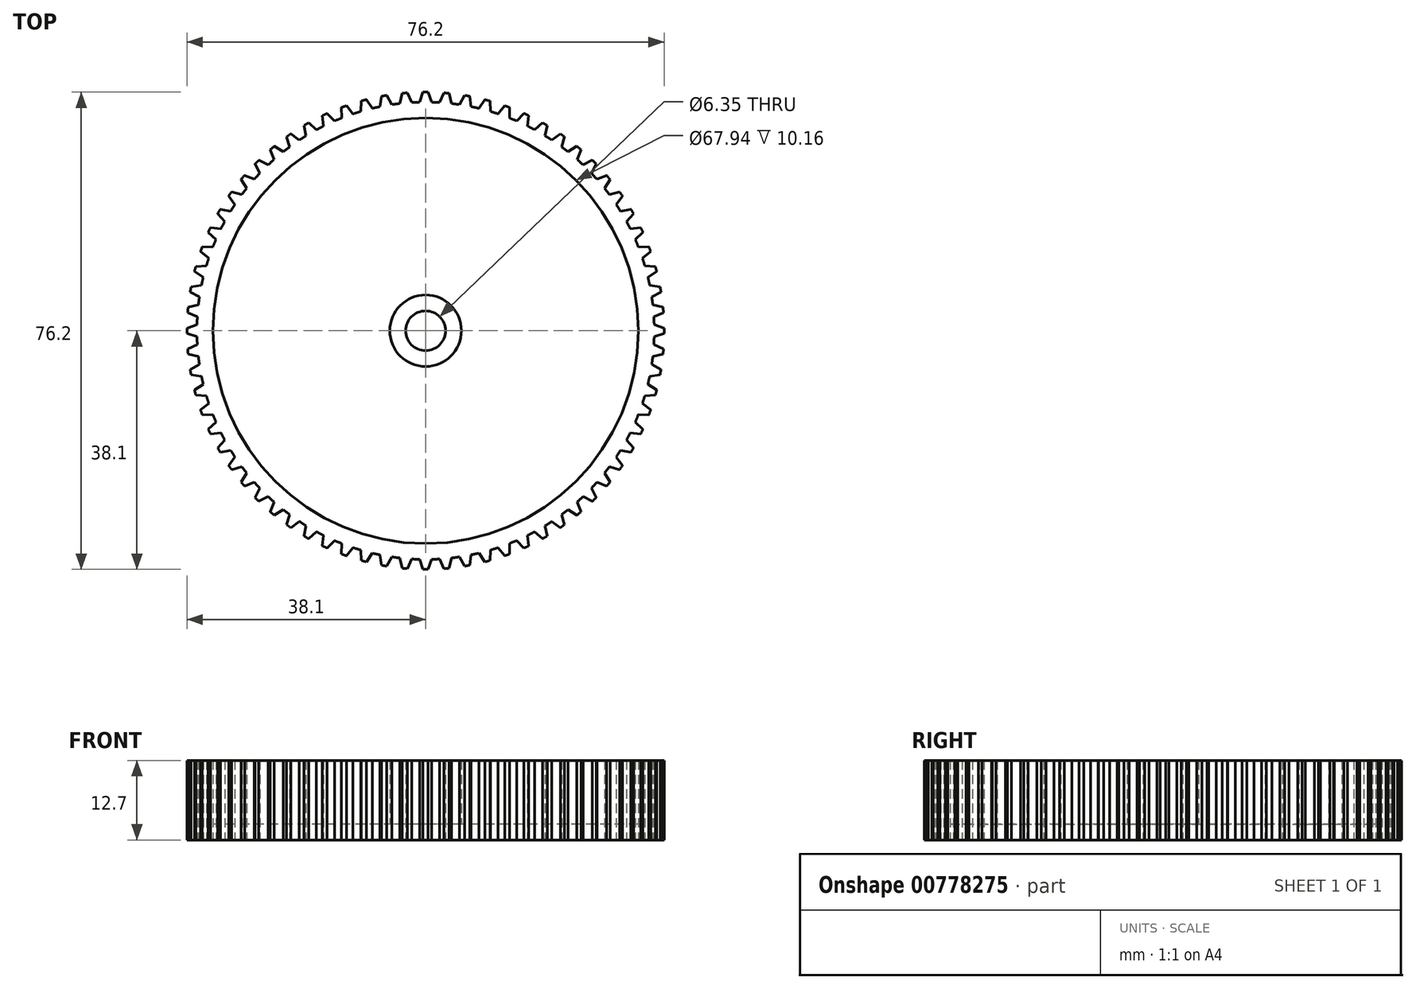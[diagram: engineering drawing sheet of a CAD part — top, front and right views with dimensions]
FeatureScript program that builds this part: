
annotation { "Feature Type Name" : "Feature", "Feature Type Description" : "" }
export const myFeature = defineFeature(function(context is Context, id is Id, definition is map)
    precondition{}
    {
        {
            var Q0;
            Q0=qCreatedBy(makeId("Top.planeOp"),FACE);
            var sketch = newSketch(context, id + "F0", { "sketchPlane" : qUnion([Q0])});
            skCircle(sketch, "E0", {"center": v(0, 0) * mm, "radius": 38.1 * mm, "construction": true});
            skCircle(sketch, "E1", {"center": v(0, 0) * mm, "radius": 3.18 * mm});
            skLineSegment(sketch, "E2", {"start": v(0, 0) * mm, "end": v(0, 49.35) * mm, "construction": true});
            skLineSegment(sketch, "E3", {"start": v(0, 0) * mm, "end": v(-2.1, 47.97) * mm, "construction": true});
            skLineSegment(sketch, "E4", {"start": v(0, 0) * mm, "end": v(2.15, 49.24) * mm, "construction": true});
            skArc(sketch, "E5", {"start": v(-1.6, 36.48) * mm, "mid": v(-1.27, 36.5) * mm, "end": v(-0.96, 36.5) * mm});
            skArc(sketch, "E6", {"start": v(1.6, 36.48) * mm, "mid": v(1.27, 36.5) * mm, "end": v(0.96, 36.5) * mm});
            skLineSegment(sketch, "E7", {"start": v(-0.96, 36.5) * mm, "end": v(-0.42, 38.1) * mm});
            skLineSegment(sketch, "E8", {"start": v(0.96, 36.5) * mm, "end": v(0.42, 38.1) * mm});
            skArc(sketch, "E9", {"start": v(0.42, 38.1) * mm, "mid": v(0, 38.1) * mm, "end": v(-0.42, 38.1) * mm});
            skLineSegment(sketch, "E10", {"start": v(0, 0) * mm, "end": v(-0.96, 36.5) * mm, "construction": true});
            skLineSegment(sketch, "E11", {"start": v(0.96, 36.5) * mm, "end": v(0, 0) * mm, "construction": true});
            skArc(sketch, "E12.1.0", {"start": v(-4.77, 36.2) * mm, "mid": v(-4.45, 36.24) * mm, "end": v(-4.13, 36.28) * mm});
            skArc(sketch, "E12.1.1", {"start": v(-2.9, 37.99) * mm, "mid": v(-3.32, 37.95) * mm, "end": v(-3.74, 37.92) * mm});
            skLineSegment(sketch, "E12.1.2", {"start": v(-4.13, 36.28) * mm, "end": v(-3.74, 37.92) * mm});
            skLineSegment(sketch, "E12.1.3", {"start": v(-2.23, 36.44) * mm, "end": v(-2.9, 37.99) * mm});
            skArc(sketch, "E12.1.4", {"start": v(-1.6, 36.48) * mm, "mid": v(-1.91, 36.46) * mm, "end": v(-2.23, 36.44) * mm});
            skArc(sketch, "E12.2.0", {"start": v(-7.9, 35.65) * mm, "mid": v(-7.6, 35.71) * mm, "end": v(-7.28, 35.78) * mm});
            skArc(sketch, "E12.2.1", {"start": v(-6.2, 37.6) * mm, "mid": v(-6.62, 37.52) * mm, "end": v(-7.03, 37.45) * mm});
            skLineSegment(sketch, "E12.2.2", {"start": v(-7.28, 35.78) * mm, "end": v(-7.03, 37.45) * mm});
            skLineSegment(sketch, "E12.2.3", {"start": v(-5.4, 36.11) * mm, "end": v(-6.2, 37.6) * mm});
            skArc(sketch, "E12.2.4", {"start": v(-4.77, 36.2) * mm, "mid": v(-5.08, 36.16) * mm, "end": v(-5.4, 36.11) * mm});
            skArc(sketch, "E12.3.0", {"start": v(-10.98, 34.82) * mm, "mid": v(-10.68, 34.92) * mm, "end": v(-10.37, 35) * mm});
            skArc(sketch, "E12.3.1", {"start": v(-9.45, 36.9) * mm, "mid": v(-9.86, 36.8) * mm, "end": v(-10.27, 36.7) * mm});
            skLineSegment(sketch, "E12.3.2", {"start": v(-10.37, 35) * mm, "end": v(-10.27, 36.7) * mm});
            skLineSegment(sketch, "E12.3.3", {"start": v(-8.52, 35.5) * mm, "end": v(-9.45, 36.9) * mm});
            skArc(sketch, "E12.3.4", {"start": v(-7.9, 35.65) * mm, "mid": v(-8.21, 35.58) * mm, "end": v(-8.52, 35.5) * mm});
            skArc(sketch, "E12.4.0", {"start": v(-13.97, 33.73) * mm, "mid": v(-13.68, 33.85) * mm, "end": v(-13.38, 33.97) * mm});
            skArc(sketch, "E12.4.1", {"start": v(-12.63, 35.94) * mm, "mid": v(-13.03, 35.8) * mm, "end": v(-13.43, 35.66) * mm});
            skLineSegment(sketch, "E12.4.2", {"start": v(-13.38, 33.97) * mm, "end": v(-13.43, 35.66) * mm});
            skLineSegment(sketch, "E12.4.3", {"start": v(-11.59, 34.63) * mm, "end": v(-12.63, 35.94) * mm});
            skArc(sketch, "E12.4.4", {"start": v(-10.98, 34.82) * mm, "mid": v(-11.28, 34.73) * mm, "end": v(-11.59, 34.63) * mm});
            skArc(sketch, "E12.5.0", {"start": v(-16.86, 32.39) * mm, "mid": v(-16.58, 32.53) * mm, "end": v(-16.3, 32.68) * mm});
            skArc(sketch, "E12.5.1", {"start": v(-15.72, 34.7) * mm, "mid": v(-16.1, 34.53) * mm, "end": v(-16.48, 34.35) * mm});
            skLineSegment(sketch, "E12.5.2", {"start": v(-16.3, 32.68) * mm, "end": v(-16.48, 34.35) * mm});
            skLineSegment(sketch, "E12.5.3", {"start": v(-14.56, 33.48) * mm, "end": v(-15.72, 34.7) * mm});
            skArc(sketch, "E12.5.4", {"start": v(-13.97, 33.73) * mm, "mid": v(-14.27, 33.6) * mm, "end": v(-14.56, 33.48) * mm});
            skArc(sketch, "E12.6.0", {"start": v(-19.62, 30.8) * mm, "mid": v(-19.35, 30.96) * mm, "end": v(-19.08, 31.13) * mm});
            skArc(sketch, "E12.6.1", {"start": v(-18.68, 33.2) * mm, "mid": v(-19.05, 33) * mm, "end": v(-19.41, 32.78) * mm});
            skLineSegment(sketch, "E12.6.2", {"start": v(-19.08, 31.13) * mm, "end": v(-19.41, 32.78) * mm});
            skLineSegment(sketch, "E12.6.3", {"start": v(-17.42, 32.09) * mm, "end": v(-18.68, 33.2) * mm});
            skArc(sketch, "E12.6.4", {"start": v(-16.86, 32.39) * mm, "mid": v(-17.14, 32.24) * mm, "end": v(-17.42, 32.09) * mm});
            skArc(sketch, "E12.7.0", {"start": v(-22.23, 28.97) * mm, "mid": v(-21.97, 29.16) * mm, "end": v(-21.72, 29.35) * mm});
            skArc(sketch, "E12.7.1", {"start": v(-21.5, 31.45) * mm, "mid": v(-21.85, 31.2) * mm, "end": v(-22.2, 30.97) * mm});
            skLineSegment(sketch, "E12.7.2", {"start": v(-21.72, 29.35) * mm, "end": v(-22.2, 30.97) * mm});
            skLineSegment(sketch, "E12.7.3", {"start": v(-20.15, 30.45) * mm, "end": v(-21.5, 31.45) * mm});
            skArc(sketch, "E12.7.4", {"start": v(-19.62, 30.8) * mm, "mid": v(-19.89, 30.62) * mm, "end": v(-20.15, 30.45) * mm});
            skArc(sketch, "E12.8.0", {"start": v(-24.67, 26.92) * mm, "mid": v(-24.43, 27.13) * mm, "end": v(-24.2, 27.35) * mm});
            skArc(sketch, "E12.8.1", {"start": v(-24.17, 29.46) * mm, "mid": v(-24.49, 29.18) * mm, "end": v(-24.81, 28.91) * mm});
            skLineSegment(sketch, "E12.8.2", {"start": v(-24.2, 27.35) * mm, "end": v(-24.81, 28.91) * mm});
            skLineSegment(sketch, "E12.8.3", {"start": v(-22.73, 28.57) * mm, "end": v(-24.17, 29.46) * mm});
            skArc(sketch, "E12.8.4", {"start": v(-22.23, 28.97) * mm, "mid": v(-22.48, 28.77) * mm, "end": v(-22.73, 28.57) * mm});
            skArc(sketch, "E12.9.0", {"start": v(-26.92, 24.67) * mm, "mid": v(-26.7, 24.9) * mm, "end": v(-26.49, 25.13) * mm});
            skArc(sketch, "E12.9.1", {"start": v(-26.64, 27.24) * mm, "mid": v(-26.94, 26.94) * mm, "end": v(-27.24, 26.64) * mm});
            skLineSegment(sketch, "E12.9.2", {"start": v(-26.49, 25.13) * mm, "end": v(-27.24, 26.64) * mm});
            skLineSegment(sketch, "E12.9.3", {"start": v(-25.13, 26.49) * mm, "end": v(-26.64, 27.24) * mm});
            skArc(sketch, "E12.9.4", {"start": v(-24.67, 26.92) * mm, "mid": v(-24.9, 26.7) * mm, "end": v(-25.13, 26.49) * mm});
            skArc(sketch, "E12.10.0", {"start": v(-28.97, 22.23) * mm, "mid": v(-28.77, 22.48) * mm, "end": v(-28.57, 22.73) * mm});
            skArc(sketch, "E12.10.1", {"start": v(-28.91, 24.81) * mm, "mid": v(-29.18, 24.49) * mm, "end": v(-29.46, 24.17) * mm});
            skLineSegment(sketch, "E12.10.2", {"start": v(-28.57, 22.73) * mm, "end": v(-29.46, 24.17) * mm});
            skLineSegment(sketch, "E12.10.3", {"start": v(-27.35, 24.2) * mm, "end": v(-28.91, 24.81) * mm});
            skArc(sketch, "E12.10.4", {"start": v(-26.92, 24.67) * mm, "mid": v(-27.13, 24.43) * mm, "end": v(-27.35, 24.2) * mm});
            skArc(sketch, "E12.11.0", {"start": v(-30.8, 19.62) * mm, "mid": v(-30.62, 19.89) * mm, "end": v(-30.45, 20.15) * mm});
            skArc(sketch, "E12.11.1", {"start": v(-30.97, 22.2) * mm, "mid": v(-31.2, 21.85) * mm, "end": v(-31.45, 21.5) * mm});
            skLineSegment(sketch, "E12.11.2", {"start": v(-30.45, 20.15) * mm, "end": v(-31.45, 21.5) * mm});
            skLineSegment(sketch, "E12.11.3", {"start": v(-29.35, 21.72) * mm, "end": v(-30.97, 22.2) * mm});
            skArc(sketch, "E12.11.4", {"start": v(-28.97, 22.23) * mm, "mid": v(-29.16, 21.97) * mm, "end": v(-29.35, 21.72) * mm});
            skArc(sketch, "E12.12.0", {"start": v(-32.39, 16.86) * mm, "mid": v(-32.24, 17.14) * mm, "end": v(-32.09, 17.42) * mm});
            skArc(sketch, "E12.12.1", {"start": v(-32.78, 19.41) * mm, "mid": v(-33, 19.05) * mm, "end": v(-33.2, 18.68) * mm});
            skLineSegment(sketch, "E12.12.2", {"start": v(-32.09, 17.42) * mm, "end": v(-33.2, 18.68) * mm});
            skLineSegment(sketch, "E12.12.3", {"start": v(-31.13, 19.08) * mm, "end": v(-32.78, 19.41) * mm});
            skArc(sketch, "E12.12.4", {"start": v(-30.8, 19.62) * mm, "mid": v(-30.96, 19.35) * mm, "end": v(-31.13, 19.08) * mm});
            skArc(sketch, "E12.13.0", {"start": v(-33.73, 13.97) * mm, "mid": v(-33.6, 14.27) * mm, "end": v(-33.48, 14.56) * mm});
            skArc(sketch, "E12.13.1", {"start": v(-34.35, 16.48) * mm, "mid": v(-34.53, 16.1) * mm, "end": v(-34.7, 15.72) * mm});
            skLineSegment(sketch, "E12.13.2", {"start": v(-33.48, 14.56) * mm, "end": v(-34.7, 15.72) * mm});
            skLineSegment(sketch, "E12.13.3", {"start": v(-32.68, 16.3) * mm, "end": v(-34.35, 16.48) * mm});
            skArc(sketch, "E12.13.4", {"start": v(-32.39, 16.86) * mm, "mid": v(-32.53, 16.58) * mm, "end": v(-32.68, 16.3) * mm});
            skArc(sketch, "E12.14.0", {"start": v(-34.82, 10.98) * mm, "mid": v(-34.73, 11.28) * mm, "end": v(-34.63, 11.59) * mm});
            skArc(sketch, "E12.14.1", {"start": v(-35.66, 13.43) * mm, "mid": v(-35.8, 13.03) * mm, "end": v(-35.94, 12.63) * mm});
            skLineSegment(sketch, "E12.14.2", {"start": v(-34.63, 11.59) * mm, "end": v(-35.94, 12.63) * mm});
            skLineSegment(sketch, "E12.14.3", {"start": v(-33.97, 13.38) * mm, "end": v(-35.66, 13.43) * mm});
            skArc(sketch, "E12.14.4", {"start": v(-33.73, 13.97) * mm, "mid": v(-33.85, 13.68) * mm, "end": v(-33.97, 13.38) * mm});
            skArc(sketch, "E12.15.0", {"start": v(-35.65, 7.9) * mm, "mid": v(-35.58, 8.21) * mm, "end": v(-35.5, 8.52) * mm});
            skArc(sketch, "E12.15.1", {"start": v(-36.7, 10.27) * mm, "mid": v(-36.8, 9.86) * mm, "end": v(-36.9, 9.45) * mm});
            skLineSegment(sketch, "E12.15.2", {"start": v(-35.5, 8.52) * mm, "end": v(-36.9, 9.45) * mm});
            skLineSegment(sketch, "E12.15.3", {"start": v(-35, 10.37) * mm, "end": v(-36.7, 10.27) * mm});
            skArc(sketch, "E12.15.4", {"start": v(-34.82, 10.98) * mm, "mid": v(-34.92, 10.68) * mm, "end": v(-35, 10.37) * mm});
            skArc(sketch, "E12.16.0", {"start": v(-36.2, 4.77) * mm, "mid": v(-36.16, 5.08) * mm, "end": v(-36.11, 5.4) * mm});
            skArc(sketch, "E12.16.1", {"start": v(-37.45, 7.03) * mm, "mid": v(-37.52, 6.62) * mm, "end": v(-37.6, 6.2) * mm});
            skLineSegment(sketch, "E12.16.2", {"start": v(-36.11, 5.4) * mm, "end": v(-37.6, 6.2) * mm});
            skLineSegment(sketch, "E12.16.3", {"start": v(-35.78, 7.28) * mm, "end": v(-37.45, 7.03) * mm});
            skArc(sketch, "E12.16.4", {"start": v(-35.65, 7.9) * mm, "mid": v(-35.71, 7.6) * mm, "end": v(-35.78, 7.28) * mm});
            skArc(sketch, "E12.17.0", {"start": v(-36.48, 1.6) * mm, "mid": v(-36.46, 1.91) * mm, "end": v(-36.44, 2.23) * mm});
            skArc(sketch, "E12.17.1", {"start": v(-37.92, 3.74) * mm, "mid": v(-37.95, 3.32) * mm, "end": v(-37.99, 2.9) * mm});
            skLineSegment(sketch, "E12.17.2", {"start": v(-36.44, 2.23) * mm, "end": v(-37.99, 2.9) * mm});
            skLineSegment(sketch, "E12.17.3", {"start": v(-36.28, 4.13) * mm, "end": v(-37.92, 3.74) * mm});
            skArc(sketch, "E12.17.4", {"start": v(-36.2, 4.77) * mm, "mid": v(-36.24, 4.45) * mm, "end": v(-36.28, 4.13) * mm});
            skArc(sketch, "E12.18.0", {"start": v(-36.48, -1.6) * mm, "mid": v(-36.5, -1.27) * mm, "end": v(-36.5, -0.96) * mm});
            skArc(sketch, "E12.18.1", {"start": v(-38.1, 0.42) * mm, "mid": v(-38.1, 0) * mm, "end": v(-38.1, -0.42) * mm});
            skLineSegment(sketch, "E12.18.2", {"start": v(-36.5, -0.96) * mm, "end": v(-38.1, -0.42) * mm});
            skLineSegment(sketch, "E12.18.3", {"start": v(-36.5, 0.96) * mm, "end": v(-38.1, 0.42) * mm});
            skArc(sketch, "E12.18.4", {"start": v(-36.48, 1.6) * mm, "mid": v(-36.5, 1.27) * mm, "end": v(-36.5, 0.96) * mm});
            skArc(sketch, "E12.19.0", {"start": v(-36.2, -4.77) * mm, "mid": v(-36.24, -4.45) * mm, "end": v(-36.28, -4.13) * mm});
            skArc(sketch, "E12.19.1", {"start": v(-37.99, -2.9) * mm, "mid": v(-37.95, -3.32) * mm, "end": v(-37.92, -3.74) * mm});
            skLineSegment(sketch, "E12.19.2", {"start": v(-36.28, -4.13) * mm, "end": v(-37.92, -3.74) * mm});
            skLineSegment(sketch, "E12.19.3", {"start": v(-36.44, -2.23) * mm, "end": v(-37.99, -2.9) * mm});
            skArc(sketch, "E12.19.4", {"start": v(-36.48, -1.6) * mm, "mid": v(-36.46, -1.91) * mm, "end": v(-36.44, -2.23) * mm});
            skArc(sketch, "E12.20.0", {"start": v(-35.65, -7.9) * mm, "mid": v(-35.71, -7.6) * mm, "end": v(-35.78, -7.28) * mm});
            skArc(sketch, "E12.20.1", {"start": v(-37.6, -6.2) * mm, "mid": v(-37.52, -6.62) * mm, "end": v(-37.45, -7.03) * mm});
            skLineSegment(sketch, "E12.20.2", {"start": v(-35.78, -7.28) * mm, "end": v(-37.45, -7.03) * mm});
            skLineSegment(sketch, "E12.20.3", {"start": v(-36.11, -5.4) * mm, "end": v(-37.6, -6.2) * mm});
            skArc(sketch, "E12.20.4", {"start": v(-36.2, -4.77) * mm, "mid": v(-36.16, -5.08) * mm, "end": v(-36.11, -5.4) * mm});
            skArc(sketch, "E12.21.0", {"start": v(-34.82, -10.98) * mm, "mid": v(-34.92, -10.68) * mm, "end": v(-35, -10.37) * mm});
            skArc(sketch, "E12.21.1", {"start": v(-36.9, -9.45) * mm, "mid": v(-36.8, -9.86) * mm, "end": v(-36.7, -10.27) * mm});
            skLineSegment(sketch, "E12.21.2", {"start": v(-35, -10.37) * mm, "end": v(-36.7, -10.27) * mm});
            skLineSegment(sketch, "E12.21.3", {"start": v(-35.5, -8.52) * mm, "end": v(-36.9, -9.45) * mm});
            skArc(sketch, "E12.21.4", {"start": v(-35.65, -7.9) * mm, "mid": v(-35.58, -8.21) * mm, "end": v(-35.5, -8.52) * mm});
            skArc(sketch, "E12.22.0", {"start": v(-33.73, -13.97) * mm, "mid": v(-33.85, -13.68) * mm, "end": v(-33.97, -13.38) * mm});
            skArc(sketch, "E12.22.1", {"start": v(-35.94, -12.63) * mm, "mid": v(-35.8, -13.03) * mm, "end": v(-35.66, -13.43) * mm});
            skLineSegment(sketch, "E12.22.2", {"start": v(-33.97, -13.38) * mm, "end": v(-35.66, -13.43) * mm});
            skLineSegment(sketch, "E12.22.3", {"start": v(-34.63, -11.59) * mm, "end": v(-35.94, -12.63) * mm});
            skArc(sketch, "E12.22.4", {"start": v(-34.82, -10.98) * mm, "mid": v(-34.73, -11.28) * mm, "end": v(-34.63, -11.59) * mm});
            skArc(sketch, "E12.23.0", {"start": v(-32.39, -16.86) * mm, "mid": v(-32.53, -16.58) * mm, "end": v(-32.68, -16.3) * mm});
            skArc(sketch, "E12.23.1", {"start": v(-34.7, -15.72) * mm, "mid": v(-34.53, -16.1) * mm, "end": v(-34.35, -16.48) * mm});
            skLineSegment(sketch, "E12.23.2", {"start": v(-32.68, -16.3) * mm, "end": v(-34.35, -16.48) * mm});
            skLineSegment(sketch, "E12.23.3", {"start": v(-33.48, -14.56) * mm, "end": v(-34.7, -15.72) * mm});
            skArc(sketch, "E12.23.4", {"start": v(-33.73, -13.97) * mm, "mid": v(-33.6, -14.27) * mm, "end": v(-33.48, -14.56) * mm});
            skArc(sketch, "E12.24.0", {"start": v(-30.8, -19.62) * mm, "mid": v(-30.96, -19.35) * mm, "end": v(-31.13, -19.08) * mm});
            skArc(sketch, "E12.24.1", {"start": v(-33.2, -18.68) * mm, "mid": v(-33, -19.05) * mm, "end": v(-32.78, -19.41) * mm});
            skLineSegment(sketch, "E12.24.2", {"start": v(-31.13, -19.08) * mm, "end": v(-32.78, -19.41) * mm});
            skLineSegment(sketch, "E12.24.3", {"start": v(-32.09, -17.42) * mm, "end": v(-33.2, -18.68) * mm});
            skArc(sketch, "E12.24.4", {"start": v(-32.39, -16.86) * mm, "mid": v(-32.24, -17.14) * mm, "end": v(-32.09, -17.42) * mm});
            skArc(sketch, "E12.25.0", {"start": v(-28.97, -22.23) * mm, "mid": v(-29.16, -21.97) * mm, "end": v(-29.35, -21.72) * mm});
            skArc(sketch, "E12.25.1", {"start": v(-31.45, -21.5) * mm, "mid": v(-31.2, -21.85) * mm, "end": v(-30.97, -22.2) * mm});
            skLineSegment(sketch, "E12.25.2", {"start": v(-29.35, -21.72) * mm, "end": v(-30.97, -22.2) * mm});
            skLineSegment(sketch, "E12.25.3", {"start": v(-30.45, -20.15) * mm, "end": v(-31.45, -21.5) * mm});
            skArc(sketch, "E12.25.4", {"start": v(-30.8, -19.62) * mm, "mid": v(-30.62, -19.89) * mm, "end": v(-30.45, -20.15) * mm});
            skArc(sketch, "E12.26.0", {"start": v(-26.92, -24.67) * mm, "mid": v(-27.13, -24.43) * mm, "end": v(-27.35, -24.2) * mm});
            skArc(sketch, "E12.26.1", {"start": v(-29.46, -24.17) * mm, "mid": v(-29.18, -24.49) * mm, "end": v(-28.91, -24.81) * mm});
            skLineSegment(sketch, "E12.26.2", {"start": v(-27.35, -24.2) * mm, "end": v(-28.91, -24.81) * mm});
            skLineSegment(sketch, "E12.26.3", {"start": v(-28.57, -22.73) * mm, "end": v(-29.46, -24.17) * mm});
            skArc(sketch, "E12.26.4", {"start": v(-28.97, -22.23) * mm, "mid": v(-28.77, -22.48) * mm, "end": v(-28.57, -22.73) * mm});
            skArc(sketch, "E12.27.0", {"start": v(-24.67, -26.92) * mm, "mid": v(-24.9, -26.7) * mm, "end": v(-25.13, -26.49) * mm});
            skArc(sketch, "E12.27.1", {"start": v(-27.24, -26.64) * mm, "mid": v(-26.94, -26.94) * mm, "end": v(-26.64, -27.24) * mm});
            skLineSegment(sketch, "E12.27.2", {"start": v(-25.13, -26.49) * mm, "end": v(-26.64, -27.24) * mm});
            skLineSegment(sketch, "E12.27.3", {"start": v(-26.49, -25.13) * mm, "end": v(-27.24, -26.64) * mm});
            skArc(sketch, "E12.27.4", {"start": v(-26.92, -24.67) * mm, "mid": v(-26.7, -24.9) * mm, "end": v(-26.49, -25.13) * mm});
            skArc(sketch, "E12.28.0", {"start": v(-22.23, -28.97) * mm, "mid": v(-22.48, -28.77) * mm, "end": v(-22.73, -28.57) * mm});
            skArc(sketch, "E12.28.1", {"start": v(-24.81, -28.91) * mm, "mid": v(-24.49, -29.18) * mm, "end": v(-24.17, -29.46) * mm});
            skLineSegment(sketch, "E12.28.2", {"start": v(-22.73, -28.57) * mm, "end": v(-24.17, -29.46) * mm});
            skLineSegment(sketch, "E12.28.3", {"start": v(-24.2, -27.35) * mm, "end": v(-24.81, -28.91) * mm});
            skArc(sketch, "E12.28.4", {"start": v(-24.67, -26.92) * mm, "mid": v(-24.43, -27.13) * mm, "end": v(-24.2, -27.35) * mm});
            skArc(sketch, "E12.29.0", {"start": v(-19.62, -30.8) * mm, "mid": v(-19.89, -30.62) * mm, "end": v(-20.15, -30.45) * mm});
            skArc(sketch, "E12.29.1", {"start": v(-22.2, -30.97) * mm, "mid": v(-21.85, -31.2) * mm, "end": v(-21.5, -31.45) * mm});
            skLineSegment(sketch, "E12.29.2", {"start": v(-20.15, -30.45) * mm, "end": v(-21.5, -31.45) * mm});
            skLineSegment(sketch, "E12.29.3", {"start": v(-21.72, -29.35) * mm, "end": v(-22.2, -30.97) * mm});
            skArc(sketch, "E12.29.4", {"start": v(-22.23, -28.97) * mm, "mid": v(-21.97, -29.16) * mm, "end": v(-21.72, -29.35) * mm});
            skArc(sketch, "E12.30.0", {"start": v(-16.86, -32.39) * mm, "mid": v(-17.14, -32.24) * mm, "end": v(-17.42, -32.09) * mm});
            skArc(sketch, "E12.30.1", {"start": v(-19.41, -32.78) * mm, "mid": v(-19.05, -33) * mm, "end": v(-18.68, -33.2) * mm});
            skLineSegment(sketch, "E12.30.2", {"start": v(-17.42, -32.09) * mm, "end": v(-18.68, -33.2) * mm});
            skLineSegment(sketch, "E12.30.3", {"start": v(-19.08, -31.13) * mm, "end": v(-19.41, -32.78) * mm});
            skArc(sketch, "E12.30.4", {"start": v(-19.62, -30.8) * mm, "mid": v(-19.35, -30.96) * mm, "end": v(-19.08, -31.13) * mm});
            skArc(sketch, "E12.31.0", {"start": v(-13.97, -33.73) * mm, "mid": v(-14.27, -33.6) * mm, "end": v(-14.56, -33.48) * mm});
            skArc(sketch, "E12.31.1", {"start": v(-16.48, -34.35) * mm, "mid": v(-16.1, -34.53) * mm, "end": v(-15.72, -34.7) * mm});
            skLineSegment(sketch, "E12.31.2", {"start": v(-14.56, -33.48) * mm, "end": v(-15.72, -34.7) * mm});
            skLineSegment(sketch, "E12.31.3", {"start": v(-16.3, -32.68) * mm, "end": v(-16.48, -34.35) * mm});
            skArc(sketch, "E12.31.4", {"start": v(-16.86, -32.39) * mm, "mid": v(-16.58, -32.53) * mm, "end": v(-16.3, -32.68) * mm});
            skArc(sketch, "E12.32.0", {"start": v(-10.98, -34.82) * mm, "mid": v(-11.28, -34.73) * mm, "end": v(-11.59, -34.63) * mm});
            skArc(sketch, "E12.32.1", {"start": v(-13.43, -35.66) * mm, "mid": v(-13.03, -35.8) * mm, "end": v(-12.63, -35.94) * mm});
            skLineSegment(sketch, "E12.32.2", {"start": v(-11.59, -34.63) * mm, "end": v(-12.63, -35.94) * mm});
            skLineSegment(sketch, "E12.32.3", {"start": v(-13.38, -33.97) * mm, "end": v(-13.43, -35.66) * mm});
            skArc(sketch, "E12.32.4", {"start": v(-13.97, -33.73) * mm, "mid": v(-13.68, -33.85) * mm, "end": v(-13.38, -33.97) * mm});
            skArc(sketch, "E12.33.0", {"start": v(-7.9, -35.65) * mm, "mid": v(-8.21, -35.58) * mm, "end": v(-8.52, -35.5) * mm});
            skArc(sketch, "E12.33.1", {"start": v(-10.27, -36.7) * mm, "mid": v(-9.86, -36.8) * mm, "end": v(-9.45, -36.9) * mm});
            skLineSegment(sketch, "E12.33.2", {"start": v(-8.52, -35.5) * mm, "end": v(-9.45, -36.9) * mm});
            skLineSegment(sketch, "E12.33.3", {"start": v(-10.37, -35) * mm, "end": v(-10.27, -36.7) * mm});
            skArc(sketch, "E12.33.4", {"start": v(-10.98, -34.82) * mm, "mid": v(-10.68, -34.92) * mm, "end": v(-10.37, -35) * mm});
            skArc(sketch, "E12.34.0", {"start": v(-4.77, -36.2) * mm, "mid": v(-5.08, -36.16) * mm, "end": v(-5.4, -36.11) * mm});
            skArc(sketch, "E12.34.1", {"start": v(-7.03, -37.45) * mm, "mid": v(-6.62, -37.52) * mm, "end": v(-6.2, -37.6) * mm});
            skLineSegment(sketch, "E12.34.2", {"start": v(-5.4, -36.11) * mm, "end": v(-6.2, -37.6) * mm});
            skLineSegment(sketch, "E12.34.3", {"start": v(-7.28, -35.78) * mm, "end": v(-7.03, -37.45) * mm});
            skArc(sketch, "E12.34.4", {"start": v(-7.9, -35.65) * mm, "mid": v(-7.6, -35.71) * mm, "end": v(-7.28, -35.78) * mm});
            skArc(sketch, "E12.35.0", {"start": v(-1.6, -36.48) * mm, "mid": v(-1.91, -36.46) * mm, "end": v(-2.23, -36.44) * mm});
            skArc(sketch, "E12.35.1", {"start": v(-3.74, -37.92) * mm, "mid": v(-3.32, -37.95) * mm, "end": v(-2.9, -37.99) * mm});
            skLineSegment(sketch, "E12.35.2", {"start": v(-2.23, -36.44) * mm, "end": v(-2.9, -37.99) * mm});
            skLineSegment(sketch, "E12.35.3", {"start": v(-4.13, -36.28) * mm, "end": v(-3.74, -37.92) * mm});
            skArc(sketch, "E12.35.4", {"start": v(-4.77, -36.2) * mm, "mid": v(-4.45, -36.24) * mm, "end": v(-4.13, -36.28) * mm});
            skArc(sketch, "E12.36.0", {"start": v(1.6, -36.48) * mm, "mid": v(1.27, -36.5) * mm, "end": v(0.96, -36.5) * mm});
            skArc(sketch, "E12.36.1", {"start": v(-0.42, -38.1) * mm, "mid": v(0, -38.1) * mm, "end": v(0.42, -38.1) * mm});
            skLineSegment(sketch, "E12.36.2", {"start": v(0.96, -36.5) * mm, "end": v(0.42, -38.1) * mm});
            skLineSegment(sketch, "E12.36.3", {"start": v(-0.96, -36.5) * mm, "end": v(-0.42, -38.1) * mm});
            skArc(sketch, "E12.36.4", {"start": v(-1.6, -36.48) * mm, "mid": v(-1.27, -36.5) * mm, "end": v(-0.96, -36.5) * mm});
            skArc(sketch, "E12.37.0", {"start": v(4.77, -36.2) * mm, "mid": v(4.45, -36.24) * mm, "end": v(4.13, -36.28) * mm});
            skArc(sketch, "E12.37.1", {"start": v(2.9, -37.99) * mm, "mid": v(3.32, -37.95) * mm, "end": v(3.74, -37.92) * mm});
            skLineSegment(sketch, "E12.37.2", {"start": v(4.13, -36.28) * mm, "end": v(3.74, -37.92) * mm});
            skLineSegment(sketch, "E12.37.3", {"start": v(2.23, -36.44) * mm, "end": v(2.9, -37.99) * mm});
            skArc(sketch, "E12.37.4", {"start": v(1.6, -36.48) * mm, "mid": v(1.91, -36.46) * mm, "end": v(2.23, -36.44) * mm});
            skArc(sketch, "E12.38.0", {"start": v(7.9, -35.65) * mm, "mid": v(7.6, -35.71) * mm, "end": v(7.28, -35.78) * mm});
            skArc(sketch, "E12.38.1", {"start": v(6.2, -37.6) * mm, "mid": v(6.62, -37.52) * mm, "end": v(7.03, -37.45) * mm});
            skLineSegment(sketch, "E12.38.2", {"start": v(7.28, -35.78) * mm, "end": v(7.03, -37.45) * mm});
            skLineSegment(sketch, "E12.38.3", {"start": v(5.4, -36.11) * mm, "end": v(6.2, -37.6) * mm});
            skArc(sketch, "E12.38.4", {"start": v(4.77, -36.2) * mm, "mid": v(5.08, -36.16) * mm, "end": v(5.4, -36.11) * mm});
            skArc(sketch, "E12.39.0", {"start": v(10.98, -34.82) * mm, "mid": v(10.68, -34.92) * mm, "end": v(10.37, -35) * mm});
            skArc(sketch, "E12.39.1", {"start": v(9.45, -36.9) * mm, "mid": v(9.86, -36.8) * mm, "end": v(10.27, -36.7) * mm});
            skLineSegment(sketch, "E12.39.2", {"start": v(10.37, -35) * mm, "end": v(10.27, -36.7) * mm});
            skLineSegment(sketch, "E12.39.3", {"start": v(8.52, -35.5) * mm, "end": v(9.45, -36.9) * mm});
            skArc(sketch, "E12.39.4", {"start": v(7.9, -35.65) * mm, "mid": v(8.21, -35.58) * mm, "end": v(8.52, -35.5) * mm});
            skArc(sketch, "E12.40.0", {"start": v(13.97, -33.73) * mm, "mid": v(13.68, -33.85) * mm, "end": v(13.38, -33.97) * mm});
            skArc(sketch, "E12.40.1", {"start": v(12.63, -35.94) * mm, "mid": v(13.03, -35.8) * mm, "end": v(13.43, -35.66) * mm});
            skLineSegment(sketch, "E12.40.2", {"start": v(13.38, -33.97) * mm, "end": v(13.43, -35.66) * mm});
            skLineSegment(sketch, "E12.40.3", {"start": v(11.59, -34.63) * mm, "end": v(12.63, -35.94) * mm});
            skArc(sketch, "E12.40.4", {"start": v(10.98, -34.82) * mm, "mid": v(11.28, -34.73) * mm, "end": v(11.59, -34.63) * mm});
            skArc(sketch, "E12.41.0", {"start": v(16.86, -32.39) * mm, "mid": v(16.58, -32.53) * mm, "end": v(16.3, -32.68) * mm});
            skArc(sketch, "E12.41.1", {"start": v(15.72, -34.7) * mm, "mid": v(16.1, -34.53) * mm, "end": v(16.48, -34.35) * mm});
            skLineSegment(sketch, "E12.41.2", {"start": v(16.3, -32.68) * mm, "end": v(16.48, -34.35) * mm});
            skLineSegment(sketch, "E12.41.3", {"start": v(14.56, -33.48) * mm, "end": v(15.72, -34.7) * mm});
            skArc(sketch, "E12.41.4", {"start": v(13.97, -33.73) * mm, "mid": v(14.27, -33.6) * mm, "end": v(14.56, -33.48) * mm});
            skArc(sketch, "E12.42.0", {"start": v(19.62, -30.8) * mm, "mid": v(19.35, -30.96) * mm, "end": v(19.08, -31.13) * mm});
            skArc(sketch, "E12.42.1", {"start": v(18.68, -33.2) * mm, "mid": v(19.05, -33) * mm, "end": v(19.41, -32.78) * mm});
            skLineSegment(sketch, "E12.42.2", {"start": v(19.08, -31.13) * mm, "end": v(19.41, -32.78) * mm});
            skLineSegment(sketch, "E12.42.3", {"start": v(17.42, -32.09) * mm, "end": v(18.68, -33.2) * mm});
            skArc(sketch, "E12.42.4", {"start": v(16.86, -32.39) * mm, "mid": v(17.14, -32.24) * mm, "end": v(17.42, -32.09) * mm});
            skArc(sketch, "E12.43.0", {"start": v(22.23, -28.97) * mm, "mid": v(21.97, -29.16) * mm, "end": v(21.72, -29.35) * mm});
            skArc(sketch, "E12.43.1", {"start": v(21.5, -31.45) * mm, "mid": v(21.85, -31.2) * mm, "end": v(22.2, -30.97) * mm});
            skLineSegment(sketch, "E12.43.2", {"start": v(21.72, -29.35) * mm, "end": v(22.2, -30.97) * mm});
            skLineSegment(sketch, "E12.43.3", {"start": v(20.15, -30.45) * mm, "end": v(21.5, -31.45) * mm});
            skArc(sketch, "E12.43.4", {"start": v(19.62, -30.8) * mm, "mid": v(19.89, -30.62) * mm, "end": v(20.15, -30.45) * mm});
            skArc(sketch, "E12.44.0", {"start": v(24.67, -26.92) * mm, "mid": v(24.43, -27.13) * mm, "end": v(24.2, -27.35) * mm});
            skArc(sketch, "E12.44.1", {"start": v(24.17, -29.46) * mm, "mid": v(24.49, -29.18) * mm, "end": v(24.81, -28.91) * mm});
            skLineSegment(sketch, "E12.44.2", {"start": v(24.2, -27.35) * mm, "end": v(24.81, -28.91) * mm});
            skLineSegment(sketch, "E12.44.3", {"start": v(22.73, -28.57) * mm, "end": v(24.17, -29.46) * mm});
            skArc(sketch, "E12.44.4", {"start": v(22.23, -28.97) * mm, "mid": v(22.48, -28.77) * mm, "end": v(22.73, -28.57) * mm});
            skArc(sketch, "E12.45.0", {"start": v(26.92, -24.67) * mm, "mid": v(26.7, -24.9) * mm, "end": v(26.49, -25.13) * mm});
            skArc(sketch, "E12.45.1", {"start": v(26.64, -27.24) * mm, "mid": v(26.94, -26.94) * mm, "end": v(27.24, -26.64) * mm});
            skLineSegment(sketch, "E12.45.2", {"start": v(26.49, -25.13) * mm, "end": v(27.24, -26.64) * mm});
            skLineSegment(sketch, "E12.45.3", {"start": v(25.13, -26.49) * mm, "end": v(26.64, -27.24) * mm});
            skArc(sketch, "E12.45.4", {"start": v(24.67, -26.92) * mm, "mid": v(24.9, -26.7) * mm, "end": v(25.13, -26.49) * mm});
            skArc(sketch, "E12.46.0", {"start": v(28.97, -22.23) * mm, "mid": v(28.77, -22.48) * mm, "end": v(28.57, -22.73) * mm});
            skArc(sketch, "E12.46.1", {"start": v(28.91, -24.81) * mm, "mid": v(29.18, -24.49) * mm, "end": v(29.46, -24.17) * mm});
            skLineSegment(sketch, "E12.46.2", {"start": v(28.57, -22.73) * mm, "end": v(29.46, -24.17) * mm});
            skLineSegment(sketch, "E12.46.3", {"start": v(27.35, -24.2) * mm, "end": v(28.91, -24.81) * mm});
            skArc(sketch, "E12.46.4", {"start": v(26.92, -24.67) * mm, "mid": v(27.13, -24.43) * mm, "end": v(27.35, -24.2) * mm});
            skArc(sketch, "E12.47.0", {"start": v(30.8, -19.62) * mm, "mid": v(30.62, -19.89) * mm, "end": v(30.45, -20.15) * mm});
            skArc(sketch, "E12.47.1", {"start": v(30.97, -22.2) * mm, "mid": v(31.2, -21.85) * mm, "end": v(31.45, -21.5) * mm});
            skLineSegment(sketch, "E12.47.2", {"start": v(30.45, -20.15) * mm, "end": v(31.45, -21.5) * mm});
            skLineSegment(sketch, "E12.47.3", {"start": v(29.35, -21.72) * mm, "end": v(30.97, -22.2) * mm});
            skArc(sketch, "E12.47.4", {"start": v(28.97, -22.23) * mm, "mid": v(29.16, -21.97) * mm, "end": v(29.35, -21.72) * mm});
            skArc(sketch, "E12.48.0", {"start": v(32.39, -16.86) * mm, "mid": v(32.24, -17.14) * mm, "end": v(32.09, -17.42) * mm});
            skArc(sketch, "E12.48.1", {"start": v(32.78, -19.41) * mm, "mid": v(33, -19.05) * mm, "end": v(33.2, -18.68) * mm});
            skLineSegment(sketch, "E12.48.2", {"start": v(32.09, -17.42) * mm, "end": v(33.2, -18.68) * mm});
            skLineSegment(sketch, "E12.48.3", {"start": v(31.13, -19.08) * mm, "end": v(32.78, -19.41) * mm});
            skArc(sketch, "E12.48.4", {"start": v(30.8, -19.62) * mm, "mid": v(30.96, -19.35) * mm, "end": v(31.13, -19.08) * mm});
            skArc(sketch, "E12.49.0", {"start": v(33.73, -13.97) * mm, "mid": v(33.6, -14.27) * mm, "end": v(33.48, -14.56) * mm});
            skArc(sketch, "E12.49.1", {"start": v(34.35, -16.48) * mm, "mid": v(34.53, -16.1) * mm, "end": v(34.7, -15.72) * mm});
            skLineSegment(sketch, "E12.49.2", {"start": v(33.48, -14.56) * mm, "end": v(34.7, -15.72) * mm});
            skLineSegment(sketch, "E12.49.3", {"start": v(32.68, -16.3) * mm, "end": v(34.35, -16.48) * mm});
            skArc(sketch, "E12.49.4", {"start": v(32.39, -16.86) * mm, "mid": v(32.53, -16.58) * mm, "end": v(32.68, -16.3) * mm});
            skArc(sketch, "E12.50.0", {"start": v(34.82, -10.98) * mm, "mid": v(34.73, -11.28) * mm, "end": v(34.63, -11.59) * mm});
            skArc(sketch, "E12.50.1", {"start": v(35.66, -13.43) * mm, "mid": v(35.8, -13.03) * mm, "end": v(35.94, -12.63) * mm});
            skLineSegment(sketch, "E12.50.2", {"start": v(34.63, -11.59) * mm, "end": v(35.94, -12.63) * mm});
            skLineSegment(sketch, "E12.50.3", {"start": v(33.97, -13.38) * mm, "end": v(35.66, -13.43) * mm});
            skArc(sketch, "E12.50.4", {"start": v(33.73, -13.97) * mm, "mid": v(33.85, -13.68) * mm, "end": v(33.97, -13.38) * mm});
            skArc(sketch, "E12.51.0", {"start": v(35.65, -7.9) * mm, "mid": v(35.58, -8.21) * mm, "end": v(35.5, -8.52) * mm});
            skArc(sketch, "E12.51.1", {"start": v(36.7, -10.27) * mm, "mid": v(36.8, -9.86) * mm, "end": v(36.9, -9.45) * mm});
            skLineSegment(sketch, "E12.51.2", {"start": v(35.5, -8.52) * mm, "end": v(36.9, -9.45) * mm});
            skLineSegment(sketch, "E12.51.3", {"start": v(35, -10.37) * mm, "end": v(36.7, -10.27) * mm});
            skArc(sketch, "E12.51.4", {"start": v(34.82, -10.98) * mm, "mid": v(34.92, -10.68) * mm, "end": v(35, -10.37) * mm});
            skArc(sketch, "E12.52.0", {"start": v(36.2, -4.77) * mm, "mid": v(36.16, -5.08) * mm, "end": v(36.11, -5.4) * mm});
            skArc(sketch, "E12.52.1", {"start": v(37.45, -7.03) * mm, "mid": v(37.52, -6.62) * mm, "end": v(37.6, -6.2) * mm});
            skLineSegment(sketch, "E12.52.2", {"start": v(36.11, -5.4) * mm, "end": v(37.6, -6.2) * mm});
            skLineSegment(sketch, "E12.52.3", {"start": v(35.78, -7.28) * mm, "end": v(37.45, -7.03) * mm});
            skArc(sketch, "E12.52.4", {"start": v(35.65, -7.9) * mm, "mid": v(35.71, -7.6) * mm, "end": v(35.78, -7.28) * mm});
            skArc(sketch, "E12.53.0", {"start": v(36.48, -1.6) * mm, "mid": v(36.46, -1.91) * mm, "end": v(36.44, -2.23) * mm});
            skArc(sketch, "E12.53.1", {"start": v(37.92, -3.74) * mm, "mid": v(37.95, -3.32) * mm, "end": v(37.99, -2.9) * mm});
            skLineSegment(sketch, "E12.53.2", {"start": v(36.44, -2.23) * mm, "end": v(37.99, -2.9) * mm});
            skLineSegment(sketch, "E12.53.3", {"start": v(36.28, -4.13) * mm, "end": v(37.92, -3.74) * mm});
            skArc(sketch, "E12.53.4", {"start": v(36.2, -4.77) * mm, "mid": v(36.24, -4.45) * mm, "end": v(36.28, -4.13) * mm});
            skArc(sketch, "E12.54.0", {"start": v(36.48, 1.6) * mm, "mid": v(36.5, 1.27) * mm, "end": v(36.5, 0.96) * mm});
            skArc(sketch, "E12.54.1", {"start": v(38.1, -0.42) * mm, "mid": v(38.1, 0) * mm, "end": v(38.1, 0.42) * mm});
            skLineSegment(sketch, "E12.54.2", {"start": v(36.5, 0.96) * mm, "end": v(38.1, 0.42) * mm});
            skLineSegment(sketch, "E12.54.3", {"start": v(36.5, -0.96) * mm, "end": v(38.1, -0.42) * mm});
            skArc(sketch, "E12.54.4", {"start": v(36.48, -1.6) * mm, "mid": v(36.5, -1.27) * mm, "end": v(36.5, -0.96) * mm});
            skArc(sketch, "E12.55.0", {"start": v(36.2, 4.77) * mm, "mid": v(36.24, 4.45) * mm, "end": v(36.28, 4.13) * mm});
            skArc(sketch, "E12.55.1", {"start": v(37.99, 2.9) * mm, "mid": v(37.95, 3.32) * mm, "end": v(37.92, 3.74) * mm});
            skLineSegment(sketch, "E12.55.2", {"start": v(36.28, 4.13) * mm, "end": v(37.92, 3.74) * mm});
            skLineSegment(sketch, "E12.55.3", {"start": v(36.44, 2.23) * mm, "end": v(37.99, 2.9) * mm});
            skArc(sketch, "E12.55.4", {"start": v(36.48, 1.6) * mm, "mid": v(36.46, 1.91) * mm, "end": v(36.44, 2.23) * mm});
            skArc(sketch, "E12.56.0", {"start": v(35.65, 7.9) * mm, "mid": v(35.71, 7.6) * mm, "end": v(35.78, 7.28) * mm});
            skArc(sketch, "E12.56.1", {"start": v(37.6, 6.2) * mm, "mid": v(37.52, 6.62) * mm, "end": v(37.45, 7.03) * mm});
            skLineSegment(sketch, "E12.56.2", {"start": v(35.78, 7.28) * mm, "end": v(37.45, 7.03) * mm});
            skLineSegment(sketch, "E12.56.3", {"start": v(36.11, 5.4) * mm, "end": v(37.6, 6.2) * mm});
            skArc(sketch, "E12.56.4", {"start": v(36.2, 4.77) * mm, "mid": v(36.16, 5.08) * mm, "end": v(36.11, 5.4) * mm});
            skArc(sketch, "E12.57.0", {"start": v(34.82, 10.98) * mm, "mid": v(34.92, 10.68) * mm, "end": v(35, 10.37) * mm});
            skArc(sketch, "E12.57.1", {"start": v(36.9, 9.45) * mm, "mid": v(36.8, 9.86) * mm, "end": v(36.7, 10.27) * mm});
            skLineSegment(sketch, "E12.57.2", {"start": v(35, 10.37) * mm, "end": v(36.7, 10.27) * mm});
            skLineSegment(sketch, "E12.57.3", {"start": v(35.5, 8.52) * mm, "end": v(36.9, 9.45) * mm});
            skArc(sketch, "E12.57.4", {"start": v(35.65, 7.9) * mm, "mid": v(35.58, 8.21) * mm, "end": v(35.5, 8.52) * mm});
            skArc(sketch, "E12.58.0", {"start": v(33.73, 13.97) * mm, "mid": v(33.85, 13.68) * mm, "end": v(33.97, 13.38) * mm});
            skArc(sketch, "E12.58.1", {"start": v(35.94, 12.63) * mm, "mid": v(35.8, 13.03) * mm, "end": v(35.66, 13.43) * mm});
            skLineSegment(sketch, "E12.58.2", {"start": v(33.97, 13.38) * mm, "end": v(35.66, 13.43) * mm});
            skLineSegment(sketch, "E12.58.3", {"start": v(34.63, 11.59) * mm, "end": v(35.94, 12.63) * mm});
            skArc(sketch, "E12.58.4", {"start": v(34.82, 10.98) * mm, "mid": v(34.73, 11.28) * mm, "end": v(34.63, 11.59) * mm});
            skArc(sketch, "E12.59.0", {"start": v(32.39, 16.86) * mm, "mid": v(32.53, 16.58) * mm, "end": v(32.68, 16.3) * mm});
            skArc(sketch, "E12.59.1", {"start": v(34.7, 15.72) * mm, "mid": v(34.53, 16.1) * mm, "end": v(34.35, 16.48) * mm});
            skLineSegment(sketch, "E12.59.2", {"start": v(32.68, 16.3) * mm, "end": v(34.35, 16.48) * mm});
            skLineSegment(sketch, "E12.59.3", {"start": v(33.48, 14.56) * mm, "end": v(34.7, 15.72) * mm});
            skArc(sketch, "E12.59.4", {"start": v(33.73, 13.97) * mm, "mid": v(33.6, 14.27) * mm, "end": v(33.48, 14.56) * mm});
            skArc(sketch, "E12.60.0", {"start": v(30.8, 19.62) * mm, "mid": v(30.96, 19.35) * mm, "end": v(31.13, 19.08) * mm});
            skArc(sketch, "E12.60.1", {"start": v(33.2, 18.68) * mm, "mid": v(33, 19.05) * mm, "end": v(32.78, 19.41) * mm});
            skLineSegment(sketch, "E12.60.2", {"start": v(31.13, 19.08) * mm, "end": v(32.78, 19.41) * mm});
            skLineSegment(sketch, "E12.60.3", {"start": v(32.09, 17.42) * mm, "end": v(33.2, 18.68) * mm});
            skArc(sketch, "E12.60.4", {"start": v(32.39, 16.86) * mm, "mid": v(32.24, 17.14) * mm, "end": v(32.09, 17.42) * mm});
            skArc(sketch, "E12.61.0", {"start": v(28.97, 22.23) * mm, "mid": v(29.16, 21.97) * mm, "end": v(29.35, 21.72) * mm});
            skArc(sketch, "E12.61.1", {"start": v(31.45, 21.5) * mm, "mid": v(31.2, 21.85) * mm, "end": v(30.97, 22.2) * mm});
            skLineSegment(sketch, "E12.61.2", {"start": v(29.35, 21.72) * mm, "end": v(30.97, 22.2) * mm});
            skLineSegment(sketch, "E12.61.3", {"start": v(30.45, 20.15) * mm, "end": v(31.45, 21.5) * mm});
            skArc(sketch, "E12.61.4", {"start": v(30.8, 19.62) * mm, "mid": v(30.62, 19.89) * mm, "end": v(30.45, 20.15) * mm});
            skArc(sketch, "E12.62.0", {"start": v(26.92, 24.67) * mm, "mid": v(27.13, 24.43) * mm, "end": v(27.35, 24.2) * mm});
            skArc(sketch, "E12.62.1", {"start": v(29.46, 24.17) * mm, "mid": v(29.18, 24.49) * mm, "end": v(28.91, 24.81) * mm});
            skLineSegment(sketch, "E12.62.2", {"start": v(27.35, 24.2) * mm, "end": v(28.91, 24.81) * mm});
            skLineSegment(sketch, "E12.62.3", {"start": v(28.57, 22.73) * mm, "end": v(29.46, 24.17) * mm});
            skArc(sketch, "E12.62.4", {"start": v(28.97, 22.23) * mm, "mid": v(28.77, 22.48) * mm, "end": v(28.57, 22.73) * mm});
            skArc(sketch, "E12.63.0", {"start": v(24.67, 26.92) * mm, "mid": v(24.9, 26.7) * mm, "end": v(25.13, 26.49) * mm});
            skArc(sketch, "E12.63.1", {"start": v(27.24, 26.64) * mm, "mid": v(26.94, 26.94) * mm, "end": v(26.64, 27.24) * mm});
            skLineSegment(sketch, "E12.63.2", {"start": v(25.13, 26.49) * mm, "end": v(26.64, 27.24) * mm});
            skLineSegment(sketch, "E12.63.3", {"start": v(26.49, 25.13) * mm, "end": v(27.24, 26.64) * mm});
            skArc(sketch, "E12.63.4", {"start": v(26.92, 24.67) * mm, "mid": v(26.7, 24.9) * mm, "end": v(26.49, 25.13) * mm});
            skArc(sketch, "E12.64.0", {"start": v(22.23, 28.97) * mm, "mid": v(22.48, 28.77) * mm, "end": v(22.73, 28.57) * mm});
            skArc(sketch, "E12.64.1", {"start": v(24.81, 28.91) * mm, "mid": v(24.49, 29.18) * mm, "end": v(24.17, 29.46) * mm});
            skLineSegment(sketch, "E12.64.2", {"start": v(22.73, 28.57) * mm, "end": v(24.17, 29.46) * mm});
            skLineSegment(sketch, "E12.64.3", {"start": v(24.2, 27.35) * mm, "end": v(24.81, 28.91) * mm});
            skArc(sketch, "E12.64.4", {"start": v(24.67, 26.92) * mm, "mid": v(24.43, 27.13) * mm, "end": v(24.2, 27.35) * mm});
            skArc(sketch, "E12.65.0", {"start": v(19.62, 30.8) * mm, "mid": v(19.89, 30.62) * mm, "end": v(20.15, 30.45) * mm});
            skArc(sketch, "E12.65.1", {"start": v(22.2, 30.97) * mm, "mid": v(21.85, 31.2) * mm, "end": v(21.5, 31.45) * mm});
            skLineSegment(sketch, "E12.65.2", {"start": v(20.15, 30.45) * mm, "end": v(21.5, 31.45) * mm});
            skLineSegment(sketch, "E12.65.3", {"start": v(21.72, 29.35) * mm, "end": v(22.2, 30.97) * mm});
            skArc(sketch, "E12.65.4", {"start": v(22.23, 28.97) * mm, "mid": v(21.97, 29.16) * mm, "end": v(21.72, 29.35) * mm});
            skArc(sketch, "E12.66.0", {"start": v(16.86, 32.39) * mm, "mid": v(17.14, 32.24) * mm, "end": v(17.42, 32.09) * mm});
            skArc(sketch, "E12.66.1", {"start": v(19.41, 32.78) * mm, "mid": v(19.05, 33) * mm, "end": v(18.68, 33.2) * mm});
            skLineSegment(sketch, "E12.66.2", {"start": v(17.42, 32.09) * mm, "end": v(18.68, 33.2) * mm});
            skLineSegment(sketch, "E12.66.3", {"start": v(19.08, 31.13) * mm, "end": v(19.41, 32.78) * mm});
            skArc(sketch, "E12.66.4", {"start": v(19.62, 30.8) * mm, "mid": v(19.35, 30.96) * mm, "end": v(19.08, 31.13) * mm});
            skArc(sketch, "E12.67.0", {"start": v(13.97, 33.73) * mm, "mid": v(14.27, 33.6) * mm, "end": v(14.56, 33.48) * mm});
            skArc(sketch, "E12.67.1", {"start": v(16.48, 34.35) * mm, "mid": v(16.1, 34.53) * mm, "end": v(15.72, 34.7) * mm});
            skLineSegment(sketch, "E12.67.2", {"start": v(14.56, 33.48) * mm, "end": v(15.72, 34.7) * mm});
            skLineSegment(sketch, "E12.67.3", {"start": v(16.3, 32.68) * mm, "end": v(16.48, 34.35) * mm});
            skArc(sketch, "E12.67.4", {"start": v(16.86, 32.39) * mm, "mid": v(16.58, 32.53) * mm, "end": v(16.3, 32.68) * mm});
            skArc(sketch, "E12.68.0", {"start": v(10.98, 34.82) * mm, "mid": v(11.28, 34.73) * mm, "end": v(11.59, 34.63) * mm});
            skArc(sketch, "E12.68.1", {"start": v(13.43, 35.66) * mm, "mid": v(13.03, 35.8) * mm, "end": v(12.63, 35.94) * mm});
            skLineSegment(sketch, "E12.68.2", {"start": v(11.59, 34.63) * mm, "end": v(12.63, 35.94) * mm});
            skLineSegment(sketch, "E12.68.3", {"start": v(13.38, 33.97) * mm, "end": v(13.43, 35.66) * mm});
            skArc(sketch, "E12.68.4", {"start": v(13.97, 33.73) * mm, "mid": v(13.68, 33.85) * mm, "end": v(13.38, 33.97) * mm});
            skArc(sketch, "E12.69.0", {"start": v(7.9, 35.65) * mm, "mid": v(8.21, 35.58) * mm, "end": v(8.52, 35.5) * mm});
            skArc(sketch, "E12.69.1", {"start": v(10.27, 36.7) * mm, "mid": v(9.86, 36.8) * mm, "end": v(9.45, 36.9) * mm});
            skLineSegment(sketch, "E12.69.2", {"start": v(8.52, 35.5) * mm, "end": v(9.45, 36.9) * mm});
            skLineSegment(sketch, "E12.69.3", {"start": v(10.37, 35) * mm, "end": v(10.27, 36.7) * mm});
            skArc(sketch, "E12.69.4", {"start": v(10.98, 34.82) * mm, "mid": v(10.68, 34.92) * mm, "end": v(10.37, 35) * mm});
            skArc(sketch, "E12.70.0", {"start": v(4.77, 36.2) * mm, "mid": v(5.08, 36.16) * mm, "end": v(5.4, 36.11) * mm});
            skArc(sketch, "E12.70.1", {"start": v(7.03, 37.45) * mm, "mid": v(6.62, 37.52) * mm, "end": v(6.2, 37.6) * mm});
            skLineSegment(sketch, "E12.70.2", {"start": v(5.4, 36.11) * mm, "end": v(6.2, 37.6) * mm});
            skLineSegment(sketch, "E12.70.3", {"start": v(7.28, 35.78) * mm, "end": v(7.03, 37.45) * mm});
            skArc(sketch, "E12.70.4", {"start": v(7.9, 35.65) * mm, "mid": v(7.6, 35.71) * mm, "end": v(7.28, 35.78) * mm});
            skArc(sketch, "E12.71.0", {"start": v(1.6, 36.48) * mm, "mid": v(1.91, 36.46) * mm, "end": v(2.23, 36.44) * mm});
            skArc(sketch, "E12.71.1", {"start": v(3.74, 37.92) * mm, "mid": v(3.32, 37.95) * mm, "end": v(2.9, 37.99) * mm});
            skLineSegment(sketch, "E12.71.2", {"start": v(2.23, 36.44) * mm, "end": v(2.9, 37.99) * mm});
            skLineSegment(sketch, "E12.71.3", {"start": v(4.13, 36.28) * mm, "end": v(3.74, 37.92) * mm});
            skArc(sketch, "E12.71.4", {"start": v(4.77, 36.2) * mm, "mid": v(4.45, 36.24) * mm, "end": v(4.13, 36.28) * mm});
            skSolve(sketch);
        }
        {
            var Q0;
            Q0=makeQuery(id+"F0.imprint","IMPRINT",FACE,{"disambiguationData":[TD([[makeQuery(id+"F0.imprint","IMPRINT",EDGE,{"derivedFrom":sQuery(id+"F0.wireOp",EDGE,"E1")}),-1.0]])]});
            extrude(context, id + "F1", {"entities" : qUnion([Q0]), "depth" : 12.7 * mm, "offsetDistance" : 25.4 * mm});
        }
        {
            var Q0;
            Q0=makeQuery(id+"F1.opExtrude","CAP_FACE",FACE,{"disambiguationData":[OSD([sQuery(id+"F0.wireOp",EDGE,"E1"),sQuery(id+"F0.wireOp",EDGE,"E5"),sQuery(id+"F0.wireOp",EDGE,"E6"),sQuery(id+"F0.wireOp",EDGE,"E7"),sQuery(id+"F0.wireOp",EDGE,"E8"),sQuery(id+"F0.wireOp",EDGE,"E9"),sQuery(id+"F0.wireOp",EDGE,"E12.1.0"),sQuery(id+"F0.wireOp",EDGE,"E12.1.1"),sQuery(id+"F0.wireOp",EDGE,"E12.1.2"),sQuery(id+"F0.wireOp",EDGE,"E12.1.3"),sQuery(id+"F0.wireOp",EDGE,"E12.1.4"),sQuery(id+"F0.wireOp",EDGE,"E12.2.0"),sQuery(id+"F0.wireOp",EDGE,"E12.2.1"),sQuery(id+"F0.wireOp",EDGE,"E12.2.2"),sQuery(id+"F0.wireOp",EDGE,"E12.2.3"),sQuery(id+"F0.wireOp",EDGE,"E12.2.4"),sQuery(id+"F0.wireOp",EDGE,"E12.3.0"),sQuery(id+"F0.wireOp",EDGE,"E12.3.1"),sQuery(id+"F0.wireOp",EDGE,"E12.3.2"),sQuery(id+"F0.wireOp",EDGE,"E12.3.3"),sQuery(id+"F0.wireOp",EDGE,"E12.3.4"),sQuery(id+"F0.wireOp",EDGE,"E12.4.0"),sQuery(id+"F0.wireOp",EDGE,"E12.4.1"),sQuery(id+"F0.wireOp",EDGE,"E12.4.2"),sQuery(id+"F0.wireOp",EDGE,"E12.4.3"),sQuery(id+"F0.wireOp",EDGE,"E12.4.4"),sQuery(id+"F0.wireOp",EDGE,"E12.5.0"),sQuery(id+"F0.wireOp",EDGE,"E12.5.1"),sQuery(id+"F0.wireOp",EDGE,"E12.5.2"),sQuery(id+"F0.wireOp",EDGE,"E12.5.3"),sQuery(id+"F0.wireOp",EDGE,"E12.5.4"),sQuery(id+"F0.wireOp",EDGE,"E12.6.0"),sQuery(id+"F0.wireOp",EDGE,"E12.6.1"),sQuery(id+"F0.wireOp",EDGE,"E12.6.2"),sQuery(id+"F0.wireOp",EDGE,"E12.6.3"),sQuery(id+"F0.wireOp",EDGE,"E12.6.4"),sQuery(id+"F0.wireOp",EDGE,"E12.7.0"),sQuery(id+"F0.wireOp",EDGE,"E12.7.1"),sQuery(id+"F0.wireOp",EDGE,"E12.7.2"),sQuery(id+"F0.wireOp",EDGE,"E12.7.3"),sQuery(id+"F0.wireOp",EDGE,"E12.7.4"),sQuery(id+"F0.wireOp",EDGE,"E12.8.0"),sQuery(id+"F0.wireOp",EDGE,"E12.8.1"),sQuery(id+"F0.wireOp",EDGE,"E12.8.2"),sQuery(id+"F0.wireOp",EDGE,"E12.8.3"),sQuery(id+"F0.wireOp",EDGE,"E12.8.4"),sQuery(id+"F0.wireOp",EDGE,"E12.9.0"),sQuery(id+"F0.wireOp",EDGE,"E12.9.1"),sQuery(id+"F0.wireOp",EDGE,"E12.9.2"),sQuery(id+"F0.wireOp",EDGE,"E12.9.3"),sQuery(id+"F0.wireOp",EDGE,"E12.9.4"),sQuery(id+"F0.wireOp",EDGE,"E12.10.0"),sQuery(id+"F0.wireOp",EDGE,"E12.10.1"),sQuery(id+"F0.wireOp",EDGE,"E12.10.2"),sQuery(id+"F0.wireOp",EDGE,"E12.10.3"),sQuery(id+"F0.wireOp",EDGE,"E12.10.4"),sQuery(id+"F0.wireOp",EDGE,"E12.11.0"),sQuery(id+"F0.wireOp",EDGE,"E12.11.1"),sQuery(id+"F0.wireOp",EDGE,"E12.11.2"),sQuery(id+"F0.wireOp",EDGE,"E12.11.3"),sQuery(id+"F0.wireOp",EDGE,"E12.11.4"),sQuery(id+"F0.wireOp",EDGE,"E12.12.0"),sQuery(id+"F0.wireOp",EDGE,"E12.12.1"),sQuery(id+"F0.wireOp",EDGE,"E12.12.2"),sQuery(id+"F0.wireOp",EDGE,"E12.12.3"),sQuery(id+"F0.wireOp",EDGE,"E12.12.4"),sQuery(id+"F0.wireOp",EDGE,"E12.13.0"),sQuery(id+"F0.wireOp",EDGE,"E12.13.1"),sQuery(id+"F0.wireOp",EDGE,"E12.13.2"),sQuery(id+"F0.wireOp",EDGE,"E12.13.3"),sQuery(id+"F0.wireOp",EDGE,"E12.13.4"),sQuery(id+"F0.wireOp",EDGE,"E12.14.0"),sQuery(id+"F0.wireOp",EDGE,"E12.14.1"),sQuery(id+"F0.wireOp",EDGE,"E12.14.2"),sQuery(id+"F0.wireOp",EDGE,"E12.14.3"),sQuery(id+"F0.wireOp",EDGE,"E12.14.4"),sQuery(id+"F0.wireOp",EDGE,"E12.15.0"),sQuery(id+"F0.wireOp",EDGE,"E12.15.1"),sQuery(id+"F0.wireOp",EDGE,"E12.15.2"),sQuery(id+"F0.wireOp",EDGE,"E12.15.3"),sQuery(id+"F0.wireOp",EDGE,"E12.15.4"),sQuery(id+"F0.wireOp",EDGE,"E12.16.0"),sQuery(id+"F0.wireOp",EDGE,"E12.16.1"),sQuery(id+"F0.wireOp",EDGE,"E12.16.2"),sQuery(id+"F0.wireOp",EDGE,"E12.16.3"),sQuery(id+"F0.wireOp",EDGE,"E12.16.4"),sQuery(id+"F0.wireOp",EDGE,"E12.17.0"),sQuery(id+"F0.wireOp",EDGE,"E12.17.1"),sQuery(id+"F0.wireOp",EDGE,"E12.17.2"),sQuery(id+"F0.wireOp",EDGE,"E12.17.3"),sQuery(id+"F0.wireOp",EDGE,"E12.17.4"),sQuery(id+"F0.wireOp",EDGE,"E12.18.0"),sQuery(id+"F0.wireOp",EDGE,"E12.18.1"),sQuery(id+"F0.wireOp",EDGE,"E12.18.2"),sQuery(id+"F0.wireOp",EDGE,"E12.18.3"),sQuery(id+"F0.wireOp",EDGE,"E12.18.4"),sQuery(id+"F0.wireOp",EDGE,"E12.19.0"),sQuery(id+"F0.wireOp",EDGE,"E12.19.1"),sQuery(id+"F0.wireOp",EDGE,"E12.19.2"),sQuery(id+"F0.wireOp",EDGE,"E12.19.3"),sQuery(id+"F0.wireOp",EDGE,"E12.19.4"),sQuery(id+"F0.wireOp",EDGE,"E12.20.0"),sQuery(id+"F0.wireOp",EDGE,"E12.20.1"),sQuery(id+"F0.wireOp",EDGE,"E12.20.2"),sQuery(id+"F0.wireOp",EDGE,"E12.20.3"),sQuery(id+"F0.wireOp",EDGE,"E12.20.4"),sQuery(id+"F0.wireOp",EDGE,"E12.21.0"),sQuery(id+"F0.wireOp",EDGE,"E12.21.1"),sQuery(id+"F0.wireOp",EDGE,"E12.21.2"),sQuery(id+"F0.wireOp",EDGE,"E12.21.3"),sQuery(id+"F0.wireOp",EDGE,"E12.21.4"),sQuery(id+"F0.wireOp",EDGE,"E12.22.0"),sQuery(id+"F0.wireOp",EDGE,"E12.22.1"),sQuery(id+"F0.wireOp",EDGE,"E12.22.2"),sQuery(id+"F0.wireOp",EDGE,"E12.22.3"),sQuery(id+"F0.wireOp",EDGE,"E12.22.4"),sQuery(id+"F0.wireOp",EDGE,"E12.23.0"),sQuery(id+"F0.wireOp",EDGE,"E12.23.1"),sQuery(id+"F0.wireOp",EDGE,"E12.23.2"),sQuery(id+"F0.wireOp",EDGE,"E12.23.3"),sQuery(id+"F0.wireOp",EDGE,"E12.23.4"),sQuery(id+"F0.wireOp",EDGE,"E12.24.0"),sQuery(id+"F0.wireOp",EDGE,"E12.24.1"),sQuery(id+"F0.wireOp",EDGE,"E12.24.2"),sQuery(id+"F0.wireOp",EDGE,"E12.24.3"),sQuery(id+"F0.wireOp",EDGE,"E12.24.4"),sQuery(id+"F0.wireOp",EDGE,"E12.25.0"),sQuery(id+"F0.wireOp",EDGE,"E12.25.1"),sQuery(id+"F0.wireOp",EDGE,"E12.25.2"),sQuery(id+"F0.wireOp",EDGE,"E12.25.3"),sQuery(id+"F0.wireOp",EDGE,"E12.25.4"),sQuery(id+"F0.wireOp",EDGE,"E12.26.0"),sQuery(id+"F0.wireOp",EDGE,"E12.26.1"),sQuery(id+"F0.wireOp",EDGE,"E12.26.2"),sQuery(id+"F0.wireOp",EDGE,"E12.26.3"),sQuery(id+"F0.wireOp",EDGE,"E12.26.4"),sQuery(id+"F0.wireOp",EDGE,"E12.27.0"),sQuery(id+"F0.wireOp",EDGE,"E12.27.1"),sQuery(id+"F0.wireOp",EDGE,"E12.27.2"),sQuery(id+"F0.wireOp",EDGE,"E12.27.3"),sQuery(id+"F0.wireOp",EDGE,"E12.27.4"),sQuery(id+"F0.wireOp",EDGE,"E12.28.0"),sQuery(id+"F0.wireOp",EDGE,"E12.28.1"),sQuery(id+"F0.wireOp",EDGE,"E12.28.2"),sQuery(id+"F0.wireOp",EDGE,"E12.28.3"),sQuery(id+"F0.wireOp",EDGE,"E12.28.4"),sQuery(id+"F0.wireOp",EDGE,"E12.29.0"),sQuery(id+"F0.wireOp",EDGE,"E12.29.1"),sQuery(id+"F0.wireOp",EDGE,"E12.29.2"),sQuery(id+"F0.wireOp",EDGE,"E12.29.3"),sQuery(id+"F0.wireOp",EDGE,"E12.29.4"),sQuery(id+"F0.wireOp",EDGE,"E12.30.0"),sQuery(id+"F0.wireOp",EDGE,"E12.30.1"),sQuery(id+"F0.wireOp",EDGE,"E12.30.2"),sQuery(id+"F0.wireOp",EDGE,"E12.30.3"),sQuery(id+"F0.wireOp",EDGE,"E12.30.4"),sQuery(id+"F0.wireOp",EDGE,"E12.31.0"),sQuery(id+"F0.wireOp",EDGE,"E12.31.1"),sQuery(id+"F0.wireOp",EDGE,"E12.31.2"),sQuery(id+"F0.wireOp",EDGE,"E12.31.3"),sQuery(id+"F0.wireOp",EDGE,"E12.31.4"),sQuery(id+"F0.wireOp",EDGE,"E12.32.0"),sQuery(id+"F0.wireOp",EDGE,"E12.32.1"),sQuery(id+"F0.wireOp",EDGE,"E12.32.2"),sQuery(id+"F0.wireOp",EDGE,"E12.32.3"),sQuery(id+"F0.wireOp",EDGE,"E12.32.4"),sQuery(id+"F0.wireOp",EDGE,"E12.33.0"),sQuery(id+"F0.wireOp",EDGE,"E12.33.1"),sQuery(id+"F0.wireOp",EDGE,"E12.33.2"),sQuery(id+"F0.wireOp",EDGE,"E12.33.3"),sQuery(id+"F0.wireOp",EDGE,"E12.33.4"),sQuery(id+"F0.wireOp",EDGE,"E12.34.0"),sQuery(id+"F0.wireOp",EDGE,"E12.34.1"),sQuery(id+"F0.wireOp",EDGE,"E12.34.2"),sQuery(id+"F0.wireOp",EDGE,"E12.34.3"),sQuery(id+"F0.wireOp",EDGE,"E12.34.4"),sQuery(id+"F0.wireOp",EDGE,"E12.35.0"),sQuery(id+"F0.wireOp",EDGE,"E12.35.1"),sQuery(id+"F0.wireOp",EDGE,"E12.35.2"),sQuery(id+"F0.wireOp",EDGE,"E12.35.3"),sQuery(id+"F0.wireOp",EDGE,"E12.35.4"),sQuery(id+"F0.wireOp",EDGE,"E12.36.0"),sQuery(id+"F0.wireOp",EDGE,"E12.36.1"),sQuery(id+"F0.wireOp",EDGE,"E12.36.2"),sQuery(id+"F0.wireOp",EDGE,"E12.36.3"),sQuery(id+"F0.wireOp",EDGE,"E12.36.4"),sQuery(id+"F0.wireOp",EDGE,"E12.37.0"),sQuery(id+"F0.wireOp",EDGE,"E12.37.1"),sQuery(id+"F0.wireOp",EDGE,"E12.37.2"),sQuery(id+"F0.wireOp",EDGE,"E12.37.3"),sQuery(id+"F0.wireOp",EDGE,"E12.37.4"),sQuery(id+"F0.wireOp",EDGE,"E12.38.0"),sQuery(id+"F0.wireOp",EDGE,"E12.38.1"),sQuery(id+"F0.wireOp",EDGE,"E12.38.2"),sQuery(id+"F0.wireOp",EDGE,"E12.38.3"),sQuery(id+"F0.wireOp",EDGE,"E12.38.4"),sQuery(id+"F0.wireOp",EDGE,"E12.39.0"),sQuery(id+"F0.wireOp",EDGE,"E12.39.1"),sQuery(id+"F0.wireOp",EDGE,"E12.39.2"),sQuery(id+"F0.wireOp",EDGE,"E12.39.3"),sQuery(id+"F0.wireOp",EDGE,"E12.39.4"),sQuery(id+"F0.wireOp",EDGE,"E12.40.0"),sQuery(id+"F0.wireOp",EDGE,"E12.40.1"),sQuery(id+"F0.wireOp",EDGE,"E12.40.2"),sQuery(id+"F0.wireOp",EDGE,"E12.40.3"),sQuery(id+"F0.wireOp",EDGE,"E12.40.4"),sQuery(id+"F0.wireOp",EDGE,"E12.41.0"),sQuery(id+"F0.wireOp",EDGE,"E12.41.1"),sQuery(id+"F0.wireOp",EDGE,"E12.41.2"),sQuery(id+"F0.wireOp",EDGE,"E12.41.3"),sQuery(id+"F0.wireOp",EDGE,"E12.41.4"),sQuery(id+"F0.wireOp",EDGE,"E12.42.0"),sQuery(id+"F0.wireOp",EDGE,"E12.42.1"),sQuery(id+"F0.wireOp",EDGE,"E12.42.2"),sQuery(id+"F0.wireOp",EDGE,"E12.42.3"),sQuery(id+"F0.wireOp",EDGE,"E12.42.4"),sQuery(id+"F0.wireOp",EDGE,"E12.43.0"),sQuery(id+"F0.wireOp",EDGE,"E12.43.1"),sQuery(id+"F0.wireOp",EDGE,"E12.43.2"),sQuery(id+"F0.wireOp",EDGE,"E12.43.3"),sQuery(id+"F0.wireOp",EDGE,"E12.43.4"),sQuery(id+"F0.wireOp",EDGE,"E12.44.0"),sQuery(id+"F0.wireOp",EDGE,"E12.44.1"),sQuery(id+"F0.wireOp",EDGE,"E12.44.2"),sQuery(id+"F0.wireOp",EDGE,"E12.44.3"),sQuery(id+"F0.wireOp",EDGE,"E12.44.4"),sQuery(id+"F0.wireOp",EDGE,"E12.45.0"),sQuery(id+"F0.wireOp",EDGE,"E12.45.1"),sQuery(id+"F0.wireOp",EDGE,"E12.45.2"),sQuery(id+"F0.wireOp",EDGE,"E12.45.3"),sQuery(id+"F0.wireOp",EDGE,"E12.45.4"),sQuery(id+"F0.wireOp",EDGE,"E12.46.0"),sQuery(id+"F0.wireOp",EDGE,"E12.46.1"),sQuery(id+"F0.wireOp",EDGE,"E12.46.2"),sQuery(id+"F0.wireOp",EDGE,"E12.46.3"),sQuery(id+"F0.wireOp",EDGE,"E12.46.4"),sQuery(id+"F0.wireOp",EDGE,"E12.47.0"),sQuery(id+"F0.wireOp",EDGE,"E12.47.1"),sQuery(id+"F0.wireOp",EDGE,"E12.47.2"),sQuery(id+"F0.wireOp",EDGE,"E12.47.3"),sQuery(id+"F0.wireOp",EDGE,"E12.47.4"),sQuery(id+"F0.wireOp",EDGE,"E12.48.0"),sQuery(id+"F0.wireOp",EDGE,"E12.48.1"),sQuery(id+"F0.wireOp",EDGE,"E12.48.2"),sQuery(id+"F0.wireOp",EDGE,"E12.48.3"),sQuery(id+"F0.wireOp",EDGE,"E12.48.4"),sQuery(id+"F0.wireOp",EDGE,"E12.49.0"),sQuery(id+"F0.wireOp",EDGE,"E12.49.1"),sQuery(id+"F0.wireOp",EDGE,"E12.49.2"),sQuery(id+"F0.wireOp",EDGE,"E12.49.3"),sQuery(id+"F0.wireOp",EDGE,"E12.49.4"),sQuery(id+"F0.wireOp",EDGE,"E12.50.0"),sQuery(id+"F0.wireOp",EDGE,"E12.50.1"),sQuery(id+"F0.wireOp",EDGE,"E12.50.2"),sQuery(id+"F0.wireOp",EDGE,"E12.50.3"),sQuery(id+"F0.wireOp",EDGE,"E12.50.4"),sQuery(id+"F0.wireOp",EDGE,"E12.51.0"),sQuery(id+"F0.wireOp",EDGE,"E12.51.1"),sQuery(id+"F0.wireOp",EDGE,"E12.51.2"),sQuery(id+"F0.wireOp",EDGE,"E12.51.3"),sQuery(id+"F0.wireOp",EDGE,"E12.51.4"),sQuery(id+"F0.wireOp",EDGE,"E12.52.0"),sQuery(id+"F0.wireOp",EDGE,"E12.52.1"),sQuery(id+"F0.wireOp",EDGE,"E12.52.2"),sQuery(id+"F0.wireOp",EDGE,"E12.52.3"),sQuery(id+"F0.wireOp",EDGE,"E12.52.4"),sQuery(id+"F0.wireOp",EDGE,"E12.53.0"),sQuery(id+"F0.wireOp",EDGE,"E12.53.1"),sQuery(id+"F0.wireOp",EDGE,"E12.53.2"),sQuery(id+"F0.wireOp",EDGE,"E12.53.3"),sQuery(id+"F0.wireOp",EDGE,"E12.53.4"),sQuery(id+"F0.wireOp",EDGE,"E12.54.0"),sQuery(id+"F0.wireOp",EDGE,"E12.54.1"),sQuery(id+"F0.wireOp",EDGE,"E12.54.2"),sQuery(id+"F0.wireOp",EDGE,"E12.54.3"),sQuery(id+"F0.wireOp",EDGE,"E12.54.4"),sQuery(id+"F0.wireOp",EDGE,"E12.55.0"),sQuery(id+"F0.wireOp",EDGE,"E12.55.1"),sQuery(id+"F0.wireOp",EDGE,"E12.55.2"),sQuery(id+"F0.wireOp",EDGE,"E12.55.3"),sQuery(id+"F0.wireOp",EDGE,"E12.55.4"),sQuery(id+"F0.wireOp",EDGE,"E12.56.0"),sQuery(id+"F0.wireOp",EDGE,"E12.56.1"),sQuery(id+"F0.wireOp",EDGE,"E12.56.2"),sQuery(id+"F0.wireOp",EDGE,"E12.56.3"),sQuery(id+"F0.wireOp",EDGE,"E12.56.4"),sQuery(id+"F0.wireOp",EDGE,"E12.57.0"),sQuery(id+"F0.wireOp",EDGE,"E12.57.1"),sQuery(id+"F0.wireOp",EDGE,"E12.57.2"),sQuery(id+"F0.wireOp",EDGE,"E12.57.3"),sQuery(id+"F0.wireOp",EDGE,"E12.57.4"),sQuery(id+"F0.wireOp",EDGE,"E12.58.0"),sQuery(id+"F0.wireOp",EDGE,"E12.58.1"),sQuery(id+"F0.wireOp",EDGE,"E12.58.2"),sQuery(id+"F0.wireOp",EDGE,"E12.58.3"),sQuery(id+"F0.wireOp",EDGE,"E12.58.4"),sQuery(id+"F0.wireOp",EDGE,"E12.59.0"),sQuery(id+"F0.wireOp",EDGE,"E12.59.1"),sQuery(id+"F0.wireOp",EDGE,"E12.59.2"),sQuery(id+"F0.wireOp",EDGE,"E12.59.3"),sQuery(id+"F0.wireOp",EDGE,"E12.59.4"),sQuery(id+"F0.wireOp",EDGE,"E12.60.0"),sQuery(id+"F0.wireOp",EDGE,"E12.60.1"),sQuery(id+"F0.wireOp",EDGE,"E12.60.2"),sQuery(id+"F0.wireOp",EDGE,"E12.60.3"),sQuery(id+"F0.wireOp",EDGE,"E12.60.4"),sQuery(id+"F0.wireOp",EDGE,"E12.61.0"),sQuery(id+"F0.wireOp",EDGE,"E12.61.1"),sQuery(id+"F0.wireOp",EDGE,"E12.61.2"),sQuery(id+"F0.wireOp",EDGE,"E12.61.3"),sQuery(id+"F0.wireOp",EDGE,"E12.61.4"),sQuery(id+"F0.wireOp",EDGE,"E12.62.0"),sQuery(id+"F0.wireOp",EDGE,"E12.62.1"),sQuery(id+"F0.wireOp",EDGE,"E12.62.2"),sQuery(id+"F0.wireOp",EDGE,"E12.62.3"),sQuery(id+"F0.wireOp",EDGE,"E12.62.4"),sQuery(id+"F0.wireOp",EDGE,"E12.63.0"),sQuery(id+"F0.wireOp",EDGE,"E12.63.1"),sQuery(id+"F0.wireOp",EDGE,"E12.63.2"),sQuery(id+"F0.wireOp",EDGE,"E12.63.3"),sQuery(id+"F0.wireOp",EDGE,"E12.63.4"),sQuery(id+"F0.wireOp",EDGE,"E12.64.0"),sQuery(id+"F0.wireOp",EDGE,"E12.64.1"),sQuery(id+"F0.wireOp",EDGE,"E12.64.2"),sQuery(id+"F0.wireOp",EDGE,"E12.64.3"),sQuery(id+"F0.wireOp",EDGE,"E12.64.4"),sQuery(id+"F0.wireOp",EDGE,"E12.65.0"),sQuery(id+"F0.wireOp",EDGE,"E12.65.1"),sQuery(id+"F0.wireOp",EDGE,"E12.65.2"),sQuery(id+"F0.wireOp",EDGE,"E12.65.3"),sQuery(id+"F0.wireOp",EDGE,"E12.65.4"),sQuery(id+"F0.wireOp",EDGE,"E12.66.0"),sQuery(id+"F0.wireOp",EDGE,"E12.66.1"),sQuery(id+"F0.wireOp",EDGE,"E12.66.2"),sQuery(id+"F0.wireOp",EDGE,"E12.66.3"),sQuery(id+"F0.wireOp",EDGE,"E12.66.4"),sQuery(id+"F0.wireOp",EDGE,"E12.67.0"),sQuery(id+"F0.wireOp",EDGE,"E12.67.1"),sQuery(id+"F0.wireOp",EDGE,"E12.67.2"),sQuery(id+"F0.wireOp",EDGE,"E12.67.3"),sQuery(id+"F0.wireOp",EDGE,"E12.67.4"),sQuery(id+"F0.wireOp",EDGE,"E12.68.0"),sQuery(id+"F0.wireOp",EDGE,"E12.68.1"),sQuery(id+"F0.wireOp",EDGE,"E12.68.2"),sQuery(id+"F0.wireOp",EDGE,"E12.68.3"),sQuery(id+"F0.wireOp",EDGE,"E12.68.4"),sQuery(id+"F0.wireOp",EDGE,"E12.69.0"),sQuery(id+"F0.wireOp",EDGE,"E12.69.1"),sQuery(id+"F0.wireOp",EDGE,"E12.69.2"),sQuery(id+"F0.wireOp",EDGE,"E12.69.3"),sQuery(id+"F0.wireOp",EDGE,"E12.69.4"),sQuery(id+"F0.wireOp",EDGE,"E12.70.0"),sQuery(id+"F0.wireOp",EDGE,"E12.70.1"),sQuery(id+"F0.wireOp",EDGE,"E12.70.2"),sQuery(id+"F0.wireOp",EDGE,"E12.70.3"),sQuery(id+"F0.wireOp",EDGE,"E12.70.4"),sQuery(id+"F0.wireOp",EDGE,"E12.71.0"),sQuery(id+"F0.wireOp",EDGE,"E12.71.1"),sQuery(id+"F0.wireOp",EDGE,"E12.71.2"),sQuery(id+"F0.wireOp",EDGE,"E12.71.3"),sQuery(id+"F0.wireOp",EDGE,"E12.71.4")])],"isStart":false});
            shell(context, id + "F2", {"entities" : qUnion([Q0]), "thickness" : 2.54 * mm});
        }
    });
